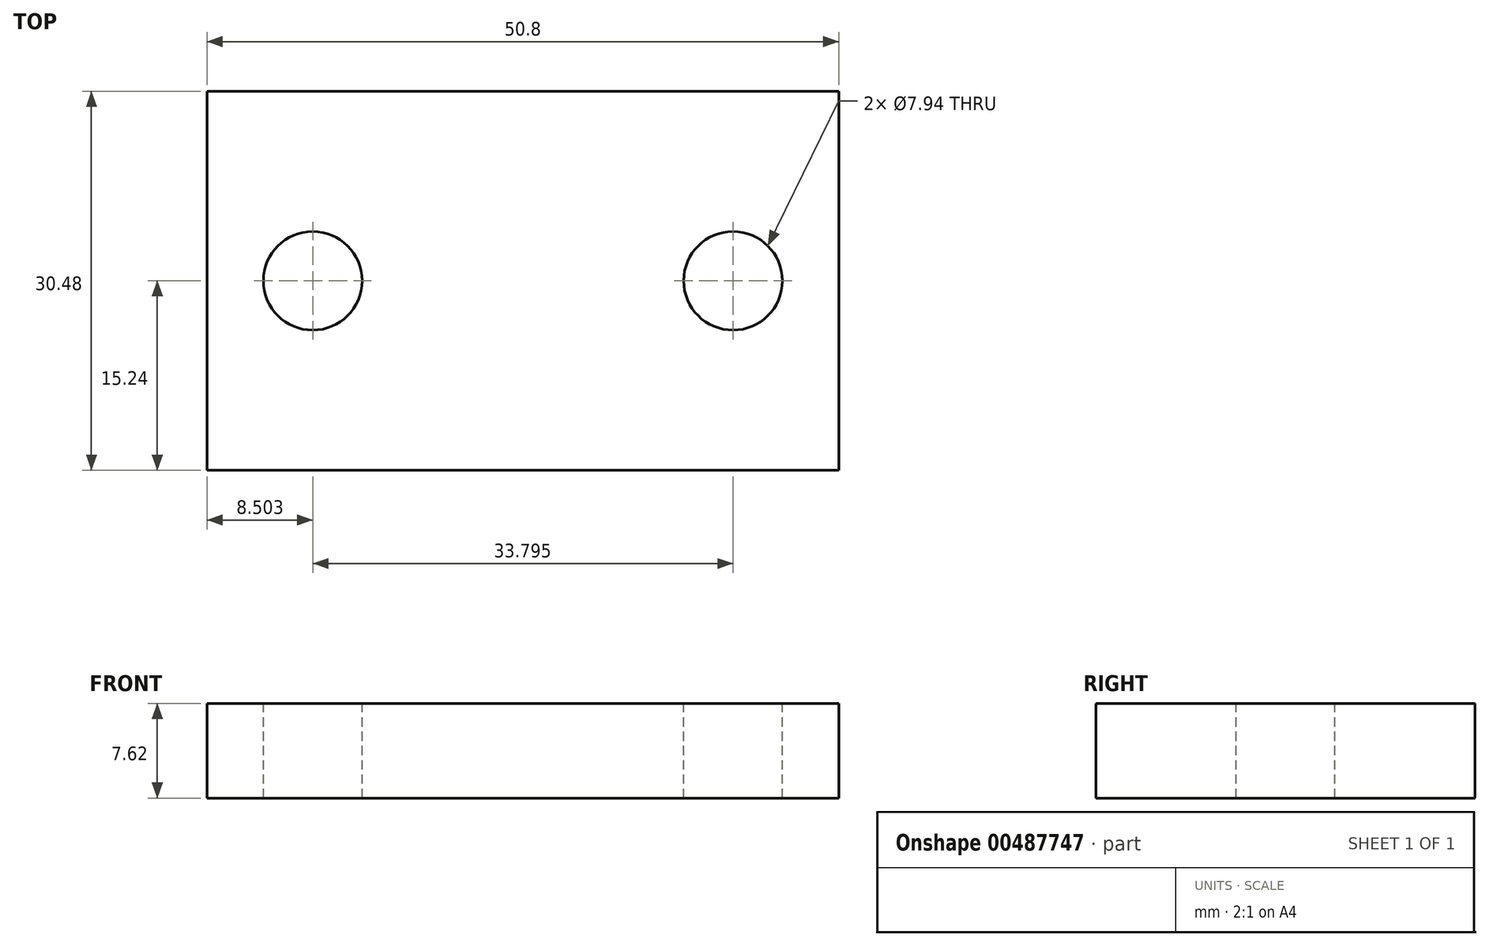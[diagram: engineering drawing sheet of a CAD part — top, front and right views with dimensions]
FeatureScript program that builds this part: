
annotation { "Feature Type Name" : "Feature", "Feature Type Description" : "" }
export const myFeature = defineFeature(function(context is Context, id is Id, definition is map)
    precondition{}
    {
        {
            var Q0;
            Q0=qCreatedBy(makeId("Top.planeOp"),FACE);
            var sketch = newSketch(context, id + "F0", { "sketchPlane" : qUnion([Q0])});
            skLineSegment(sketch, "E0.bottom", {"start": v(25.4, 15.24) * mm, "end": v(-25.4, 15.24) * mm});
            skLineSegment(sketch, "E0.top", {"start": v(25.4, -15.24) * mm, "end": v(-25.4, -15.24) * mm});
            skLineSegment(sketch, "E0.left", {"start": v(25.4, 15.24) * mm, "end": v(25.4, -15.24) * mm});
            skLineSegment(sketch, "E0.right", {"start": v(-25.4, 15.24) * mm, "end": v(-25.4, -15.24) * mm});
            skPoint(sketch, "E0.middle", {"position": v(0, 0) * mm});
            skSolve(sketch);
        }
        {
            var Q0;
            Q0=qSketchRegion(id+"F0",true);
            extrude(context, id + "F1", {"entities" : qUnion([Q0]), "depth" : 7.62 * mm});
        }
        {
            var Q0;
            Q0=makeQuery(id+"F1.opExtrude","CAP_FACE",FACE,{"disambiguationData":[OSD([sQuery(id+"F0.wireOp",EDGE,"E0.bottom"),sQuery(id+"F0.wireOp",EDGE,"E0.top"),sQuery(id+"F0.wireOp",EDGE,"E0.left"),sQuery(id+"F0.wireOp",EDGE,"E0.right")])],"isStart":false});
            var sketch = newSketch(context, id + "F2", { "sketchPlane" : qUnion([Q0])});
            skLineSegment(sketch, "E1", {"start": v(-25.4, 0) * mm, "end": v(25.4, 0) * mm, "construction": true});
            skCircle(sketch, "E2", {"center": v(-16.9, 0) * mm, "radius": 3.97 * mm});
            skCircle(sketch, "E3", {"center": v(16.9, 0) * mm, "radius": 3.97 * mm});
            skLineSegment(sketch, "E4", {"start": v(-25.4, 0) * mm, "end": v(-20.87, 0) * mm});
            skLineSegment(sketch, "E5", {"start": v(25.4, 0) * mm, "end": v(20.87, 0) * mm});
            skSolve(sketch);
        }
        {
            var Q0;
            Q0=qSketchRegion(id+"F2",true);
            extrude(context, id + "F3", {"entities" : qUnion([Q0]), "operationType" : NewBodyOperationType.REMOVE, "oppositeDirection" : true, "depth" : 25.4 * mm});
        }
    });
